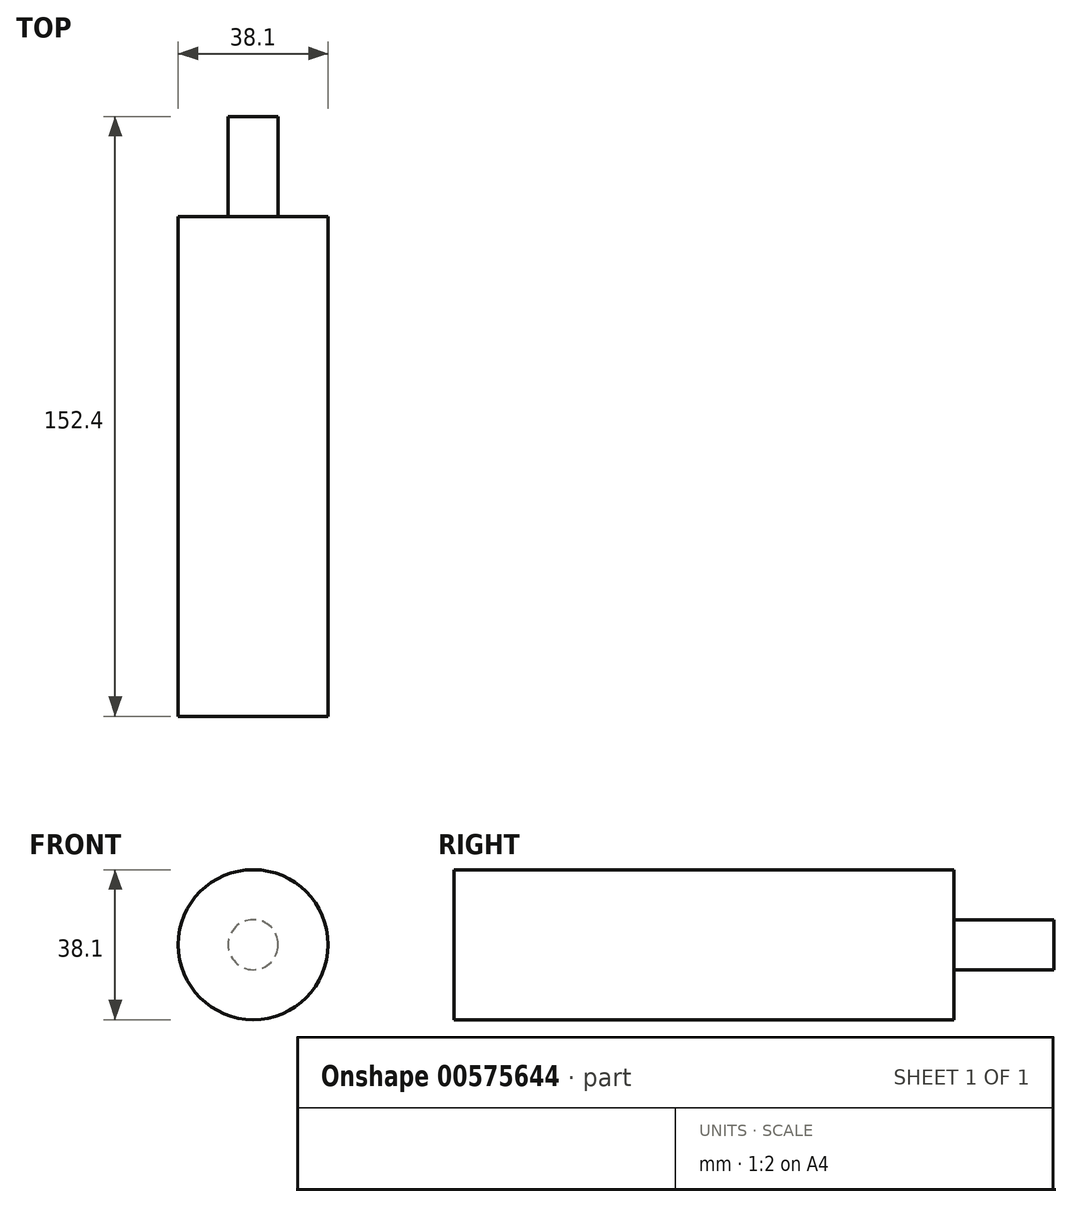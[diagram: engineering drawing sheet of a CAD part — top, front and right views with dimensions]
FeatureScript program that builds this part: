
annotation { "Feature Type Name" : "Feature", "Feature Type Description" : "" }
export const myFeature = defineFeature(function(context is Context, id is Id, definition is map)
    precondition{}
    {
        {
            var Q0;
            Q0=qCreatedBy(makeId("Front.planeOp"),FACE);
            var sketch = newSketch(context, id + "F0", { "sketchPlane" : qUnion([Q0])});
            skCircle(sketch, "E0", {"center": v(2.74, 7.53) * mm, "radius": 6.35 * mm});
            skSolve(sketch);
        }
        {
            var Q0;
            Q0=qSketchRegion(id+"F0",true);
            extrude(context, id + "F1", {"entities" : qUnion([Q0]), "depth" : 25.4 * mm, "offsetDistance" : 25.4 * mm});
        }
        {
            var Q0;
            Q0=makeQuery(id+"F1.opExtrude","CAP_FACE",FACE,{"disambiguationData":[OSD([sQuery(id+"F0.wireOp",EDGE,"E0")])],"isStart":false});
            var sketch = newSketch(context, id + "F2", { "sketchPlane" : qUnion([Q0])});
            skCircle(sketch, "E1", {"center": v(2.74, 7.53) * mm, "radius": 19.05 * mm});
            skSolve(sketch);
        }
        {
            var Q0;
            Q0=qSketchRegion(id+"F2",true);
            extrude(context, id + "F3", {"entities" : qUnion([Q0]), "operationType" : NewBodyOperationType.ADD, "depth" : 127 * mm, "offsetDistance" : 25.4 * mm});
        }
    });
